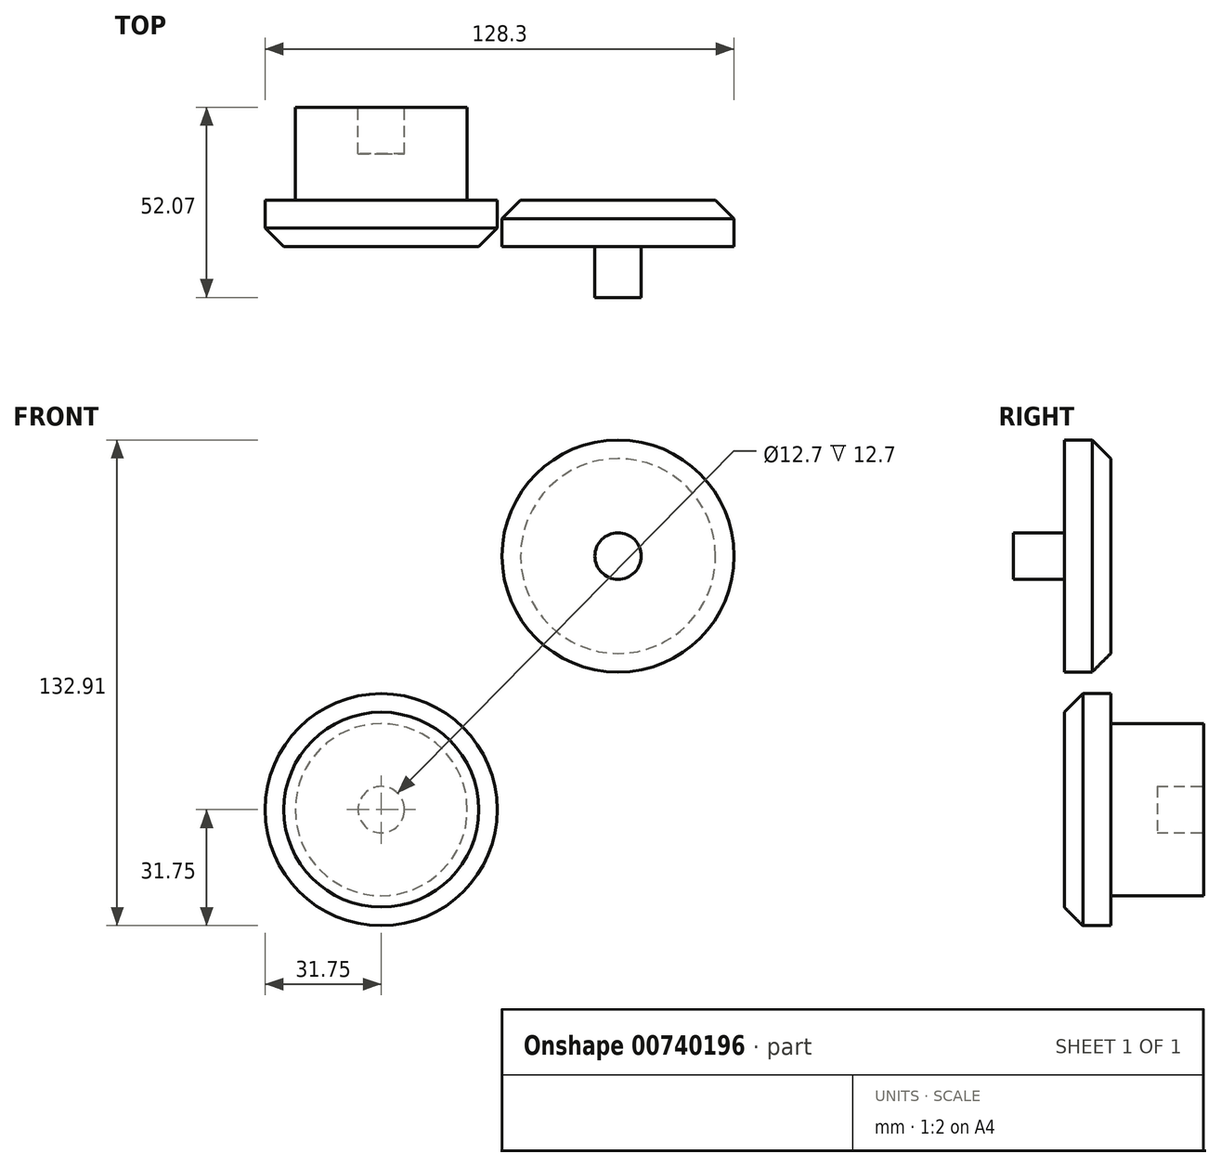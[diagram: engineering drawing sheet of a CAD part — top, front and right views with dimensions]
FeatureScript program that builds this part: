
annotation { "Feature Type Name" : "Feature", "Feature Type Description" : "" }
export const myFeature = defineFeature(function(context is Context, id is Id, definition is map)
    precondition{}
    {
        {
            var Q0;
            Q0=qCreatedBy(makeId("Front.planeOp"),FACE);
            var sketch = newSketch(context, id + "F0", { "sketchPlane" : qUnion([Q0])});
            skCircle(sketch, "E0", {"center": v(0, 0) * mm, "radius": 31.75 * mm});
            skSolve(sketch);
        }
        {
            var Q0;
            Q0 = qSketchRegion(id + "F0", true);
            extrude(context, id + "F1", {"entities" : qUnion([Q0]), "depth" : 12.7 * mm, "offsetDistance" : 25.4 * mm});
        }
        {
            var Q0;
            Q0=makeQuery(id+"F1.opExtrude","CAP_FACE",FACE,{"disambiguationData":[OSD([sQuery(id+"F0.wireOp",EDGE,"E0")])],"isStart":true});
            var sketch = newSketch(context, id + "F2", { "sketchPlane" : qUnion([Q0])});
            skCircle(sketch, "E1", {"center": v(0, 0) * mm, "radius": 23.53 * mm});
            skSolve(sketch);
        }
        {
            var Q0;
            Q0=makeQuery(id+"F2.imprint","IMPRINT",FACE,{"disambiguationData":[TD([[makeQuery(id+"F2.imprint","IMPRINT",EDGE,{"derivedFrom":sQuery(id+"F2.wireOp",EDGE,"E1")}),1.0]])]});
            extrude(context, id + "F3", {"entities" : qUnion([Q0]), "operationType" : NewBodyOperationType.ADD, "depth" : 25.4 * mm, "offsetDistance" : 25.4 * mm});
        }
        {
            var Q0;
            Q0=makeQuery(id+"F3.opExtrude","CAP_FACE",FACE,{"disambiguationData":[OSD([sQuery(id+"F2.wireOp",EDGE,"E1")])],"isStart":false});
            var sketch = newSketch(context, id + "F4", { "sketchPlane" : qUnion([Q0])});
            skCircle(sketch, "E2", {"center": v(0, 0) * mm, "radius": 6.35 * mm});
            skSolve(sketch);
        }
        {
            var Q0;
            Q0=makeQuery(id+"F4.imprint","IMPRINT",FACE,{"disambiguationData":[TD([[makeQuery(id+"F4.imprint","IMPRINT",EDGE,{"derivedFrom":sQuery(id+"F4.wireOp",EDGE,"E2")}),1.0]])]});
            extrude(context, id + "F5", {"entities" : qUnion([Q0]), "operationType" : NewBodyOperationType.REMOVE, "oppositeDirection" : true, "depth" : 12.7 * mm, "offsetDistance" : 25.4 * mm});
        }
        {
            var Q0;
            Q0=qCreatedBy(makeId("Front.planeOp"),FACE);
            var sketch = newSketch(context, id + "F6", { "sketchPlane" : qUnion([Q0])});
            skCircle(sketch, "E3", {"center": v(64.8, 69.4) * mm, "radius": 31.75 * mm});
            skSolve(sketch);
        }
        {
            var Q0;
            Q0=makeQuery(id+"F6.imprint","IMPRINT",FACE,{"disambiguationData":[TD([[makeQuery(id+"F6.imprint","IMPRINT",EDGE,{"derivedFrom":sQuery(id+"F6.wireOp",EDGE,"E3")}),1.0]])]});
            extrude(context, id + "F7", {"entities" : qUnion([Q0]), "depth" : 12.7 * mm, "offsetDistance" : 25.4 * mm});
        }
        {
            var Q0;
            Q0=makeQuery(id+"F7.opExtrude","CAP_FACE",FACE,{"disambiguationData":[OSD([sQuery(id+"F6.wireOp",EDGE,"E3")])],"isStart":false});
            var sketch = newSketch(context, id + "F8", { "sketchPlane" : qUnion([Q0])});
            skCircle(sketch, "E4", {"center": v(64.8, 69.4) * mm, "radius": 6.35 * mm});
            skSolve(sketch);
        }
        {
            var Q0;
            Q0=makeQuery(id+"F8.imprint","IMPRINT",FACE,{"disambiguationData":[TD([[makeQuery(id+"F8.imprint","IMPRINT",EDGE,{"derivedFrom":sQuery(id+"F8.wireOp",EDGE,"E4")}),1.0]])]});
            extrude(context, id + "F9", {"entities" : qUnion([Q0]), "operationType" : NewBodyOperationType.ADD, "depth" : 13.97 * mm, "offsetDistance" : 25.4 * mm});
        }
        {
            var Q0;
            Q0=makeQuery(id+"F1.opExtrude","CAP_EDGE",EDGE,{"disambiguationData":[OSD([sQuery(id+"F0.wireOp",EDGE,"E0")])],"isStart":false});
            var Q1;
            Q1=makeQuery(id+"F7.opExtrude","CAP_EDGE",EDGE,{"disambiguationData":[OSD([sQuery(id+"F6.wireOp",EDGE,"E3")])],"isStart":true});
            chamfer(context, id + "F10", {"entities" : qUnion([Q0, Q1]), "width" : 5.08 * mm, "tangentPropagation" : true});
        }
    });
